# Revit family: Legrand_Gestion_eclairage_Alimentation_Plafond_DALI
name_source: partatom
category: Dispositifs d'éclairage
units: mm (PartAtom-declared; Revit-internal decimal feet)

## family parameters
Conserver l'orientation des annotations = Non
Cote de connecteur circulaire = Utiliser le diamètre
Couper avec des vides une fois chargée = Non
Hôte = Face
Partagée = Non
Point de calcul de pièce = Non
Type d'élément = Normal

## types (2) — shared parameters
Adapté pour transmission sans fil = Non
Collecteur de terre = Non
Condition Générale d'Utilisation = https://export.legrand.com
Cosses d'artère secondaire = Non
Couleur = <Par catégorie>
Coupure forcée = Non
Elévation par défaut = 1219 mm
Fabricant = Legrand
Fonction variateur intégré = Non
Gestion CVC = Non
Gestion alarme = Non
Liaison neutre = Non
Réglage de lumière constante = Non
Sensibilité lumineuse réglable = Non
Sensibilité réglable = Non
Télécommandable = Non
URL = http://www.legrandoc.com
zero-valued in all types: Angle de détection horizontal (MAX) (°), Angle de détection horizontal (MIN) (°), Capacité de coupure max. (W), Courant de démarrage max. (A), Diamètre de détection sur le plancher (m), Durée d'enclenchement max. (mn), Durée d'enclenchement min. (s), Hauteur de montage maximale (m), Numéro RAL, Portée max. frontale (m), Portée max. latérale (m), Sensibilité lumineuse (MAX) (lx), Sensibilité lumineuse (MIN) (lx), Température (MAX) (°C), Température (MIN) (°C), Tension nominale (V)

## per-type parameters (varying)
| type | Alimentation DALI | Boite de contrôle 2 sorties DALI | Classe de protection (IP) | Description | Entrée secondaire | Exécution - Modèle | Fréquence (MAX) (Hz) | Fréquence (MIN) (Hz) | Mode de montage | Modèle |
| Alimentation DALI | Oui | Non |  | Alimentation DALI Prog Mosaic - pour variateurs colorimétriques 078403/048858/59 | Non |  | 0 | 0 | autre | 003515 |
| Boite de contrôle 2 sorties DALI | Non | Oui | IP20 | Alimentation DALI - boîtier 4 entrées /2 sorties | Oui | module de commande | 60 | 50 | apparent | 048876 |
